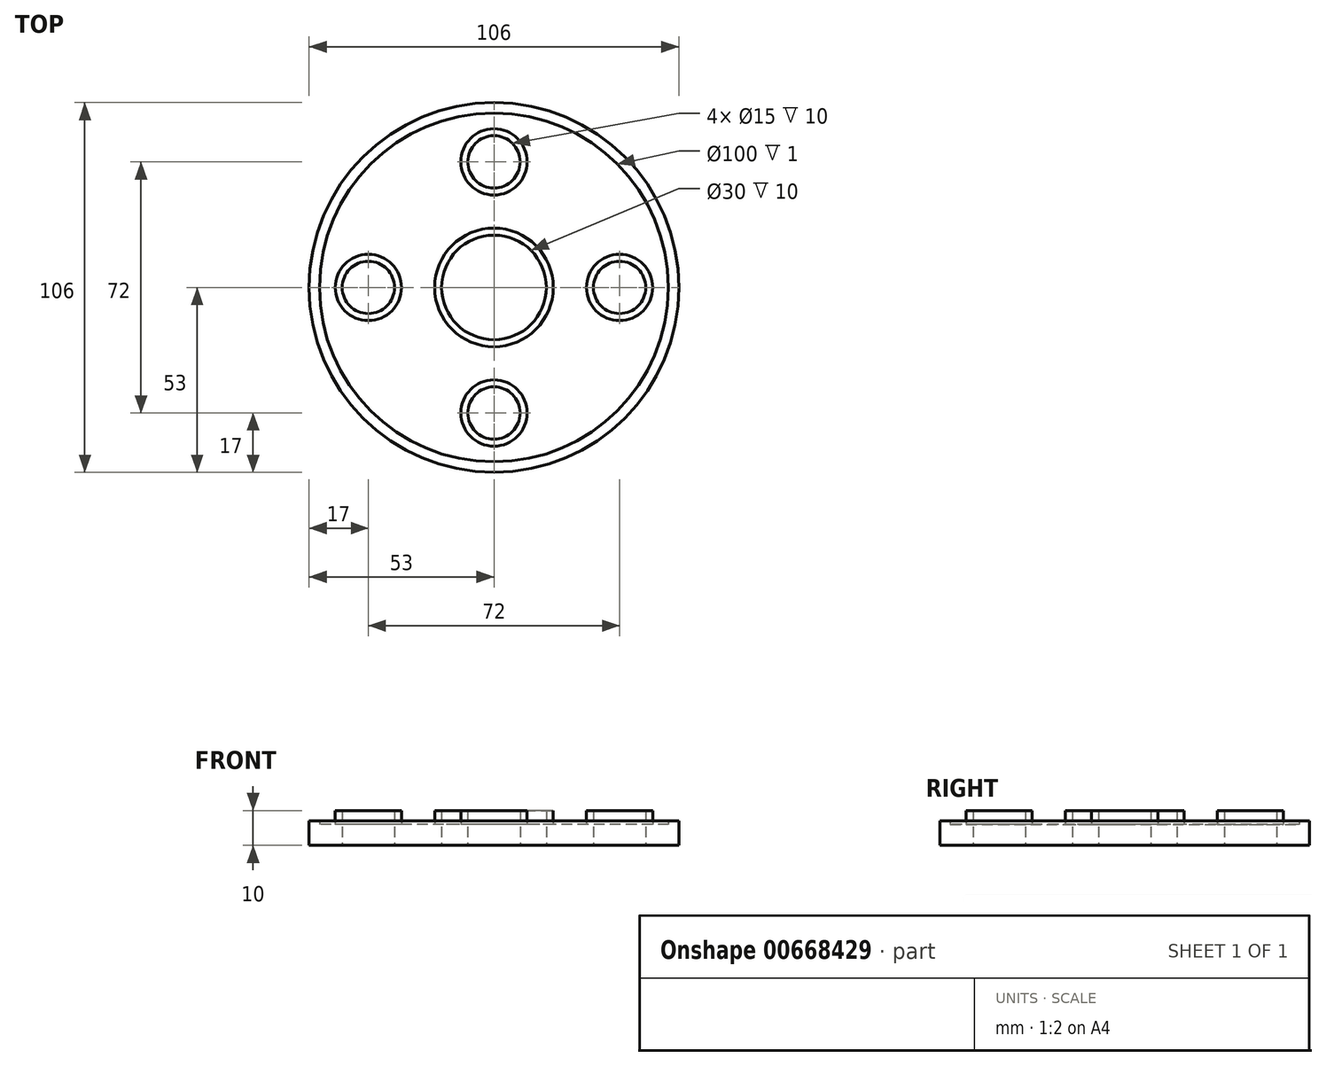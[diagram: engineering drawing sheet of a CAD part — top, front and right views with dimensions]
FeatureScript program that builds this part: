
annotation { "Feature Type Name" : "Feature", "Feature Type Description" : "" }
export const myFeature = defineFeature(function(context is Context, id is Id, definition is map)
    precondition{}
    {
        {
            var Q0;
            Q0=qCreatedBy(makeId("Top.planeOp"),FACE);
            var sketch = newSketch(context, id + "F0", { "sketchPlane" : qUnion([Q0])});
            skCircle(sketch, "E0", {"center": v(0, 0) * mm, "radius": 17 * mm});
            skCircle(sketch, "E1", {"center": v(0, 0) * mm, "radius": 15 * mm});
            skCircle(sketch, "E2", {"center": v(0, 0) * mm, "radius": 50 * mm});
            skCircle(sketch, "E3", {"center": v(0, 0) * mm, "radius": 53 * mm});
            skCircle(sketch, "E4", {"center": v(0, 36) * mm, "radius": 7.5 * mm});
            skCircle(sketch, "E5", {"center": v(0, 36) * mm, "radius": 9.5 * mm});
            skCircle(sketch, "E6.1.0", {"center": v(-36, 0) * mm, "radius": 9.5 * mm});
            skCircle(sketch, "E6.1.1", {"center": v(-36, 0) * mm, "radius": 7.5 * mm});
            skCircle(sketch, "E6.2.0", {"center": v(0, -36) * mm, "radius": 9.5 * mm});
            skCircle(sketch, "E6.2.1", {"center": v(0, -36) * mm, "radius": 7.5 * mm});
            skCircle(sketch, "E6.3.0", {"center": v(36, 0) * mm, "radius": 9.5 * mm});
            skCircle(sketch, "E6.3.1", {"center": v(36, 0) * mm, "radius": 7.5 * mm});
            skSolve(sketch);
        }
        {
            var Q0;
            Q0 = qSketchRegion(id + "F0", true);
            extrude(context, id + "F1", {"entities" : qUnion([Q0]), "depth" : 7 * mm, "offsetDistance" : 25 * mm});
        }
        {
            var Q0;
            Q0 = qSketchRegion(id + "F0", true);
            var Q1;
            Q1=makeQuery(id+"F0.imprint","IMPRINT",FACE,{"disambiguationData":[TD([[makeQuery(id+"F0.imprint","IMPRINT",EDGE,{"derivedFrom":sQuery(id+"F0.wireOp",EDGE,"E0")}),-1.0]])]});
            extrude(context, id + "F2", {"entities" : qUnion([Q0, Q1]), "operationType" : NewBodyOperationType.ADD, "depth" : 6 * mm, "offsetDistance" : 25 * mm});
        }
        {
            var Q0;
            Q0=makeQuery(id+"F0.imprint","IMPRINT",FACE,{"disambiguationData":[TD([[makeQuery(id+"F0.imprint","IMPRINT",EDGE,{"derivedFrom":sQuery(id+"F0.wireOp",EDGE,"E4")}),-1.0]])]});
            var Q1;
            Q1=makeQuery(id+"F0.imprint","IMPRINT",FACE,{"disambiguationData":[TD([[makeQuery(id+"F0.imprint","IMPRINT",EDGE,{"derivedFrom":sQuery(id+"F0.wireOp",EDGE,"E6.3.0")}),1.0]])]});
            var Q2;
            Q2=makeQuery(id+"F0.imprint","IMPRINT",FACE,{"disambiguationData":[TD([[makeQuery(id+"F0.imprint","IMPRINT",EDGE,{"derivedFrom":sQuery(id+"F0.wireOp",EDGE,"E6.1.0")}),1.0]])]});
            var Q3;
            Q3=makeQuery(id+"F0.imprint","IMPRINT",FACE,{"disambiguationData":[TD([[makeQuery(id+"F0.imprint","IMPRINT",EDGE,{"derivedFrom":sQuery(id+"F0.wireOp",EDGE,"E6.2.0")}),1.0]])]});
            var Q4;
            Q4=makeQuery(id+"F0.imprint","IMPRINT",FACE,{"disambiguationData":[TD([[makeQuery(id+"F0.imprint","IMPRINT",EDGE,{"derivedFrom":sQuery(id+"F0.wireOp",EDGE,"E0")}),1.0]])]});
            extrude(context, id + "F3", {"entities" : qUnion([Q0, Q1, Q2, Q3, Q4]), "operationType" : NewBodyOperationType.ADD, "depth" : 10 * mm, "offsetDistance" : 25 * mm});
        }
    });
